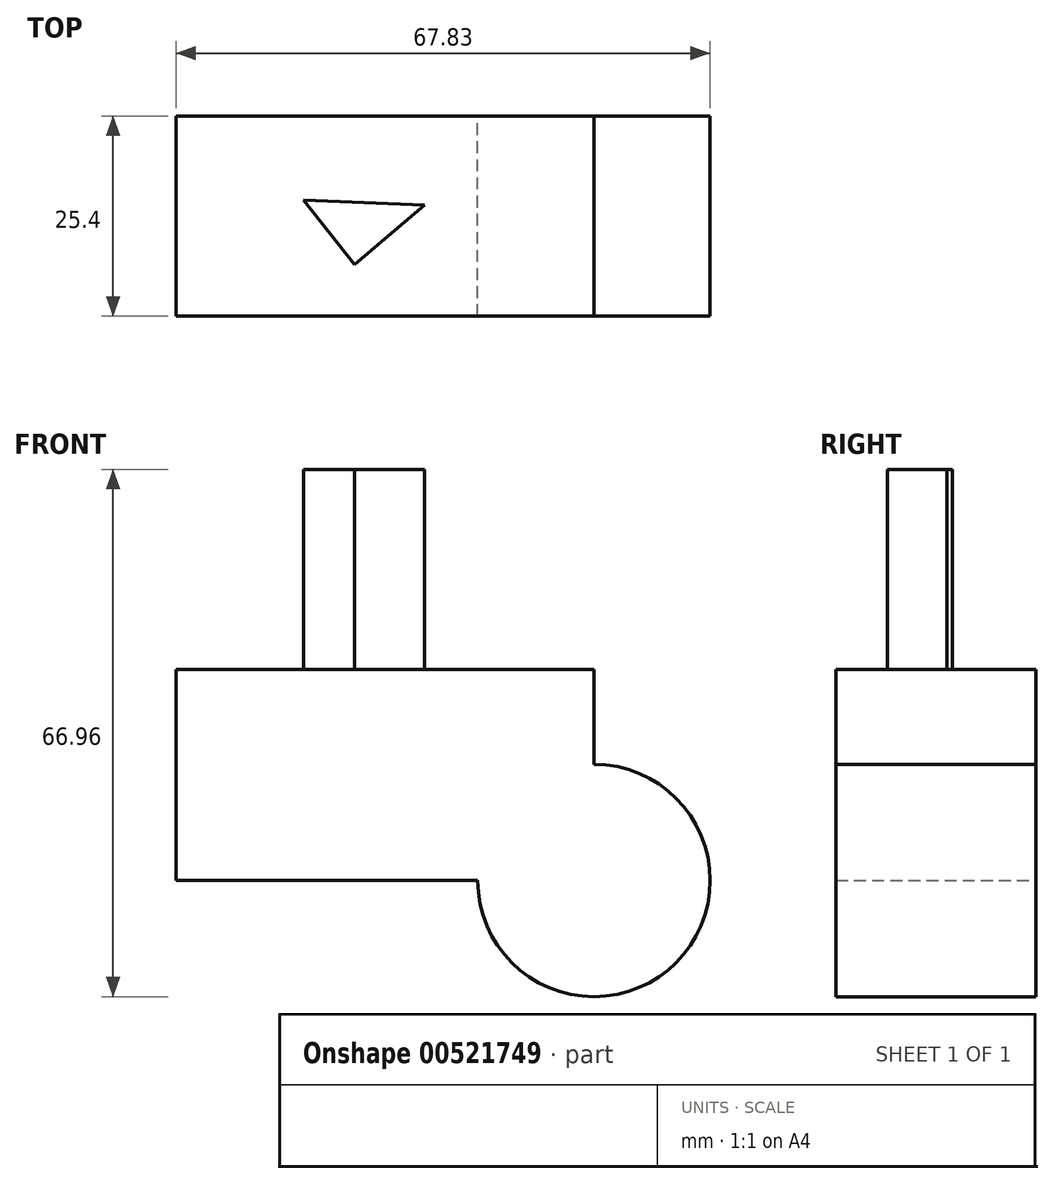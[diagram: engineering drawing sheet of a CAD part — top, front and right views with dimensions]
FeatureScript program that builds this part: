
annotation { "Feature Type Name" : "Feature", "Feature Type Description" : "" }
export const myFeature = defineFeature(function(context is Context, id is Id, definition is map)
    precondition{}
    {
        {
            var Q0;
            Q0=qCreatedBy(makeId("Front.planeOp"),FACE);
            var sketch = newSketch(context, id + "F0", { "sketchPlane" : qUnion([Q0])});
            skLineSegment(sketch, "E0.bottom", {"start": v(-35.38, 57.5) * mm, "end": v(17.7, 57.5) * mm});
            skLineSegment(sketch, "E0.top", {"start": v(-35.38, 30.7) * mm, "end": v(17.7, 30.7) * mm});
            skLineSegment(sketch, "E0.left", {"start": v(-35.38, 57.5) * mm, "end": v(-35.38, 30.7) * mm});
            skLineSegment(sketch, "E0.right", {"start": v(17.7, 57.5) * mm, "end": v(17.7, 30.7) * mm});
            skCircle(sketch, "E1", {"center": v(17.7, 30.7) * mm, "radius": 14.76 * mm});
            skSolve(sketch);
        }
        {
            var Q0;
            Q0 = qSketchRegion(id + "F0", true);
            extrude(context, id + "F1", {"entities" : qUnion([Q0]), "depth" : 25.4 * mm, "offsetDistance" : 25.4 * mm});
        }
        {
            var Q0;
            Q0=makeQuery(id+"F1.opExtrude","SWEPT_FACE",FACE,{"disambiguationData":[OSD([sQuery(id+"F0.wireOp",EDGE,"E0.bottom")])]});
            var sketch = newSketch(context, id + "F2", { "sketchPlane" : qUnion([Q0])});
            skLineSegment(sketch, "E2", {"start": v(-19.21, -10.65) * mm, "end": v(-12.7, -18.86) * mm});
            skLineSegment(sketch, "E3", {"start": v(-12.7, -18.86) * mm, "end": v(-3.84, -11.33) * mm});
            skLineSegment(sketch, "E4", {"start": v(-3.84, -11.33) * mm, "end": v(-19.21, -10.65) * mm});
            skSolve(sketch);
        }
        {
            var Q0;
            Q0 = qSketchRegion(id + "F2", true);
            extrude(context, id + "F3", {"entities" : qUnion([Q0]), "operationType" : NewBodyOperationType.ADD, "depth" : 25.4 * mm, "offsetDistance" : 25.4 * mm});
        }
    });
